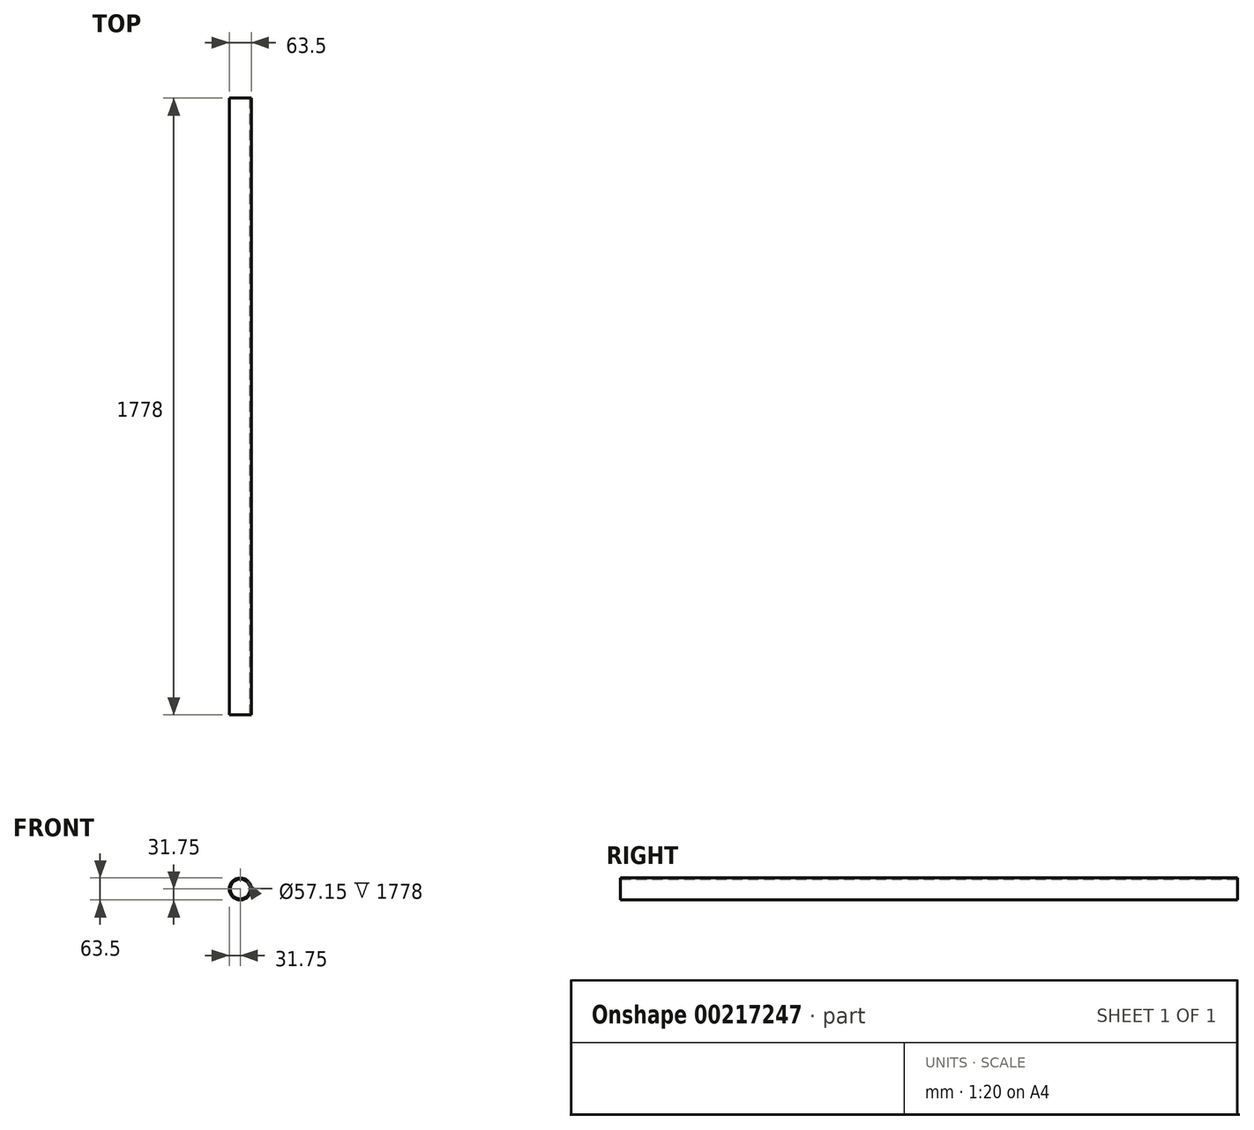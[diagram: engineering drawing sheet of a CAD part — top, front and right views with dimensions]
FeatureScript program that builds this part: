
annotation { "Feature Type Name" : "Feature", "Feature Type Description" : "" }
export const myFeature = defineFeature(function(context is Context, id is Id, definition is map)
    precondition{}
    {
        {
            var Q0;
            Q0=qCreatedBy(makeId("Front.planeOp"),FACE);
            var sketch = newSketch(context, id + "F0", { "sketchPlane" : qUnion([Q0])});
            skCircle(sketch, "E0", {"center": v(0, 0) * mm, "radius": 28.58 * mm});
            skCircle(sketch, "E1", {"center": v(0, 0) * mm, "radius": 31.75 * mm});
            skSolve(sketch);
        }
        {
            var Q0;
            Q0 = qSketchRegion(id + "F0", true);
            extrude(context, id + "F1", {"entities" : qUnion([Q0]), "depth" : 1778 * mm, "offsetDistance" : 25.4 * mm});
        }
    });
